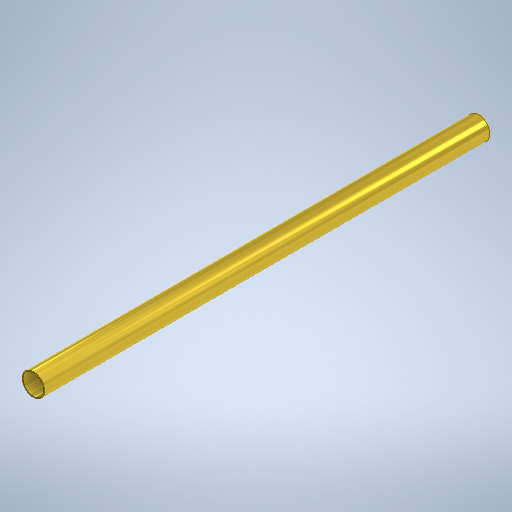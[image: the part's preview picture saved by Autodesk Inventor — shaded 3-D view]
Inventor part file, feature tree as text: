
AUTODESK INVENTOR PART (.ipt)
format: ipt  version: 2025.2 (Build 292293000, 293)  size: 252,928 bytes
history: native  units: mm
features: other x1, extrude x1, sketch x1
ambient origin geometry x8: Origin, YZ Plane, XZ Plane, XY Plane, X Axis, Y Axis, Z Axis, Center Point
bodies: Body1 (feature_tree)
feature tree (3):
  other  "Sólido1"
  extrude  "Extrusão1"  Depth=2000.0mm
  sketch  "Esboço1"  dims[d0=100.0mm d1=3.0mm d2=2000.0mm d3=0.0mm d4=0.5mm d5=0.872665mm]
